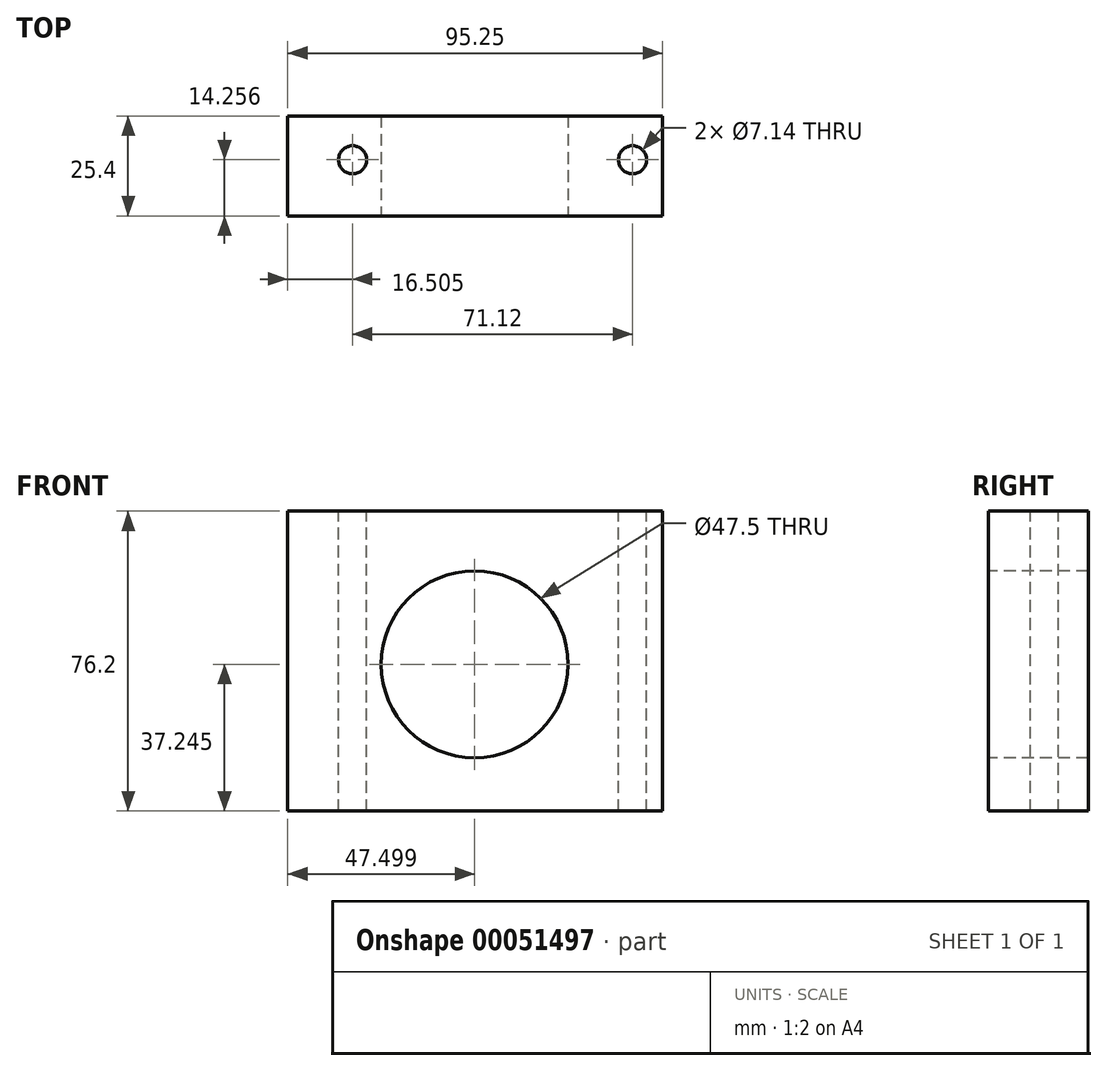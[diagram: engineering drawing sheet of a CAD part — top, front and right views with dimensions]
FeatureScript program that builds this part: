
annotation { "Feature Type Name" : "Feature", "Feature Type Description" : "" }
export const myFeature = defineFeature(function(context is Context, id is Id, definition is map)
    precondition{}
    {
        {
            var Q0;
            Q0=qCreatedBy(makeId("Front.planeOp"),FACE);
            var sketch = newSketch(context, id + "F0", { "sketchPlane" : qUnion([Q0])});
            skLineSegment(sketch, "E0.bottom", {"start": v(-69.79, 46.67) * mm, "end": v(25.46, 46.67) * mm});
            skLineSegment(sketch, "E0.top", {"start": v(-69.79, -29.53) * mm, "end": v(25.46, -29.53) * mm});
            skLineSegment(sketch, "E0.left", {"start": v(-69.79, 46.67) * mm, "end": v(-69.79, -29.53) * mm});
            skLineSegment(sketch, "E0.right", {"start": v(25.46, 46.67) * mm, "end": v(25.46, -29.53) * mm});
            skSolve(sketch);
        }
        {
            var Q0;
            Q0 = qSketchRegion(id + "F0", true);
            extrude(context, id + "F1", {"entities" : qUnion([Q0]), "depth" : 25.4 * mm});
        }
        {
            var Q0;
            Q0=makeQuery(id+"F1.opExtrude","CAP_FACE",FACE,{"disambiguationData":[OSD([sQuery(id+"F0.wireOp",EDGE,"E0.bottom"),sQuery(id+"F0.wireOp",EDGE,"E0.top"),sQuery(id+"F0.wireOp",EDGE,"E0.left"),sQuery(id+"F0.wireOp",EDGE,"E0.right")])],"isStart":false});
            var sketch = newSketch(context, id + "F2", { "sketchPlane" : qUnion([Q0])});
            skCircle(sketch, "E1", {"center": v(-22.3, 7.72) * mm, "radius": 23.75 * mm});
            skSolve(sketch);
        }
        {
            var Q0;
            Q0 = qSketchRegion(id + "F2", true);
            extrude(context, id + "F3", {"entities" : qUnion([Q0]), "operationType" : NewBodyOperationType.REMOVE, "endBound" : BoundingType.THROUGH_ALL, "oppositeDirection" : true, "depth" : 25.4 * mm});
        }
        {
            var Q0;
            Q0 = qSketchRegion(id + "F2", true);
            extrude(context, id + "F4", {"entities" : qUnion([Q0]), "operationType" : NewBodyOperationType.REMOVE, "endBound" : BoundingType.THROUGH_ALL, "oppositeDirection" : true, "depth" : 25.4 * mm});
        }
        {
            var Q0;
            Q0=makeQuery(id+"F1.opExtrude","SWEPT_FACE",FACE,{"disambiguationData":[OSD([sQuery(id+"F0.wireOp",EDGE,"E0.bottom")])]});
            var sketch = newSketch(context, id + "F5", { "sketchPlane" : qUnion([Q0])});
            skCircle(sketch, "E2", {"center": v(-53.29, -11.14) * mm, "radius": 3.57 * mm});
            skCircle(sketch, "E3", {"center": v(17.83, -11.14) * mm, "radius": 3.57 * mm});
            skSolve(sketch);
        }
        {
            var Q0;
            Q0=makeQuery(id+"F5.imprint","IMPRINT",FACE,{"disambiguationData":[TD([[makeQuery(id+"F5.imprint","IMPRINT",EDGE,{"derivedFrom":sQuery(id+"F5.wireOp",EDGE,"E3")}),1.0]])]});
            var Q1;
            Q1=makeQuery(id+"F5.imprint","IMPRINT",FACE,{"disambiguationData":[TD([[makeQuery(id+"F5.imprint","IMPRINT",EDGE,{"derivedFrom":sQuery(id+"F5.wireOp",EDGE,"E2")}),1.0]])]});
            extrude(context, id + "F6", {"entities" : qUnion([Q0, Q1]), "operationType" : NewBodyOperationType.REMOVE, "endBound" : BoundingType.THROUGH_ALL, "oppositeDirection" : true, "depth" : 91.27 * mm});
        }
    });
